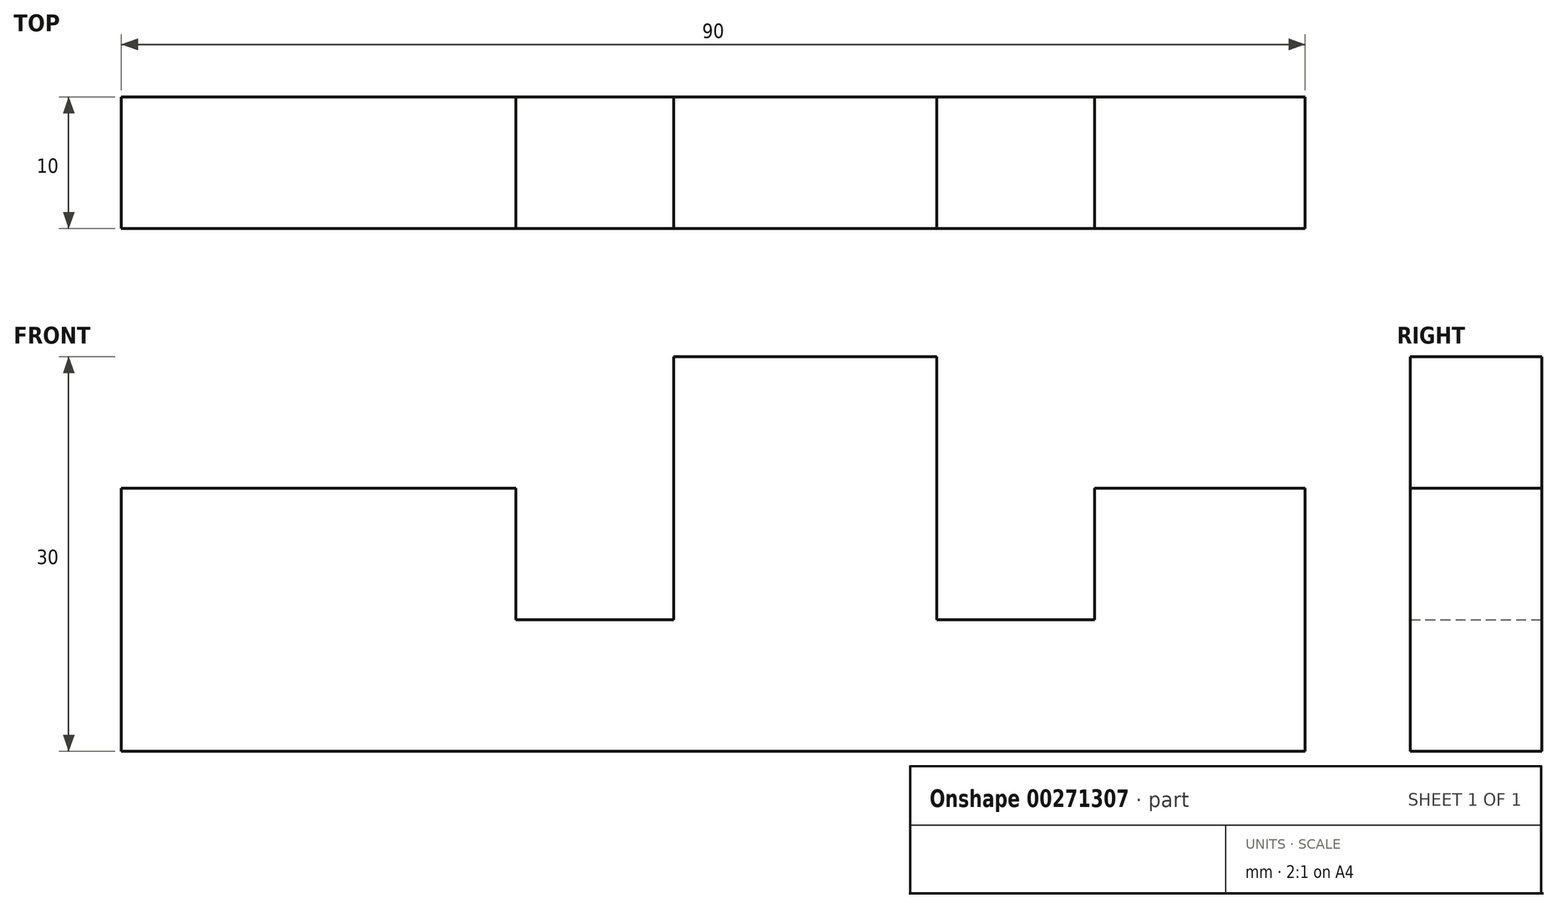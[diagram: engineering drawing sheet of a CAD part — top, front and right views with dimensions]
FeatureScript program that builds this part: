
annotation { "Feature Type Name" : "Feature", "Feature Type Description" : "" }
export const myFeature = defineFeature(function(context is Context, id is Id, definition is map)
    precondition{}
    {
        {
            var Q0;
            Q0=qCreatedBy(makeId("Front.planeOp"),FACE);
            var sketch = newSketch(context, id + "F0", { "sketchPlane" : qUnion([Q0])});
            skLineSegment(sketch, "E0", {"start": v(0, 0) * mm, "end": v(0, 20) * mm});
            skLineSegment(sketch, "E1", {"start": v(0, 20) * mm, "end": v(30, 20) * mm});
            skLineSegment(sketch, "E2", {"start": v(30, 20) * mm, "end": v(30, 10) * mm});
            skLineSegment(sketch, "E3", {"start": v(30, 10) * mm, "end": v(42, 10) * mm});
            skLineSegment(sketch, "E4", {"start": v(42, 10) * mm, "end": v(42, 30) * mm});
            skLineSegment(sketch, "E5", {"start": v(42, 30) * mm, "end": v(62, 30) * mm});
            skLineSegment(sketch, "E6", {"start": v(62, 30) * mm, "end": v(62, 10) * mm});
            skLineSegment(sketch, "E7", {"start": v(62, 10) * mm, "end": v(74, 10) * mm});
            skLineSegment(sketch, "E8", {"start": v(74, 10) * mm, "end": v(74, 20) * mm});
            skLineSegment(sketch, "E9", {"start": v(74, 20) * mm, "end": v(90, 20) * mm});
            skLineSegment(sketch, "E10", {"start": v(90, 20) * mm, "end": v(90, 0) * mm});
            skLineSegment(sketch, "E11", {"start": v(90, 0) * mm, "end": v(0, 0) * mm});
            skSolve(sketch);
        }
        {
            var Q0;
            Q0=makeQuery(id+"F0.imprint","IMPRINT",FACE,{"disambiguationData":[TD([[makeQuery(id+"F0.imprint","IMPRINT",EDGE,{"derivedFrom":sQuery(id+"F0.wireOp",EDGE,"E0")}),-1.0]])]});
            extrude(context, id + "F1", {"entities" : qUnion([Q0]), "depth" : 10 * mm});
        }
    });
